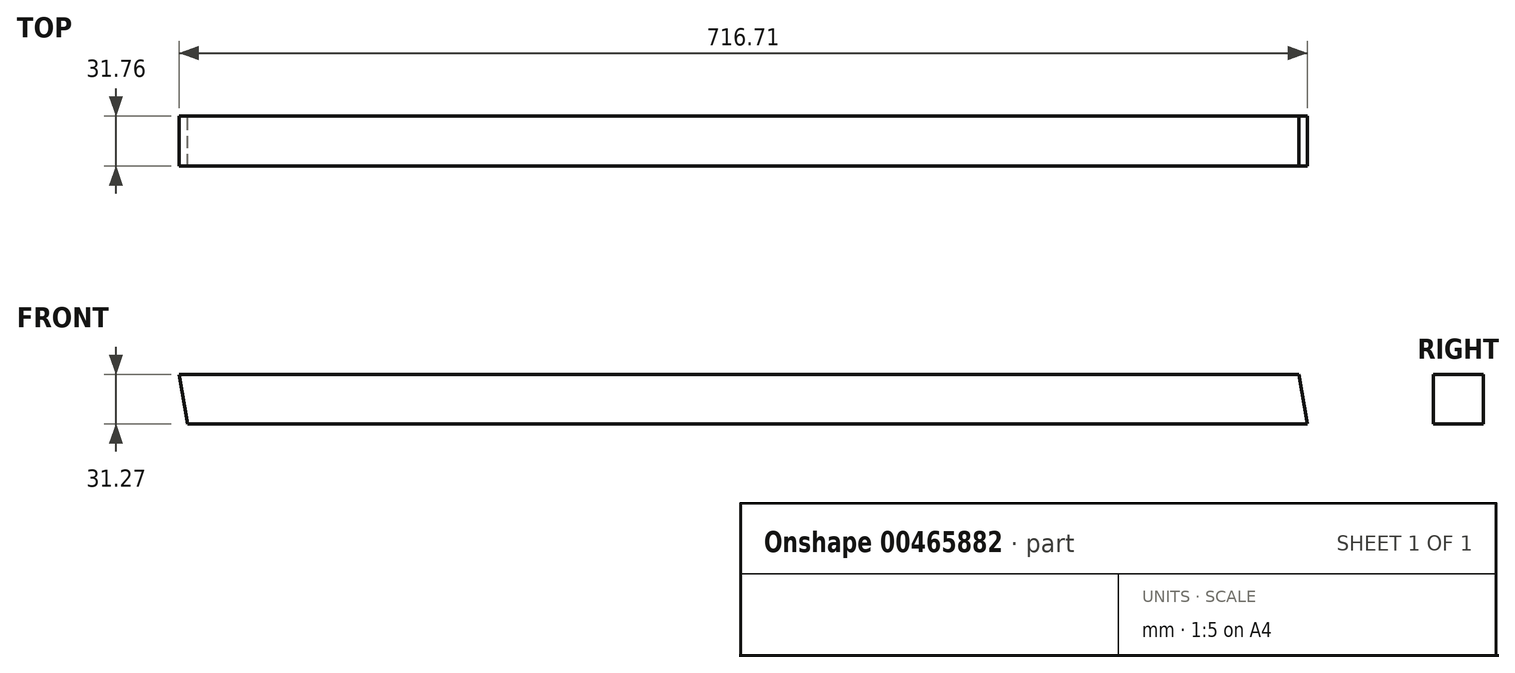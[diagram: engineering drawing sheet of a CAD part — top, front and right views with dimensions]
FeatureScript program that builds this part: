
annotation { "Feature Type Name" : "Feature", "Feature Type Description" : "" }
export const myFeature = defineFeature(function(context is Context, id is Id, definition is map)
    precondition{}
    {
        {
            var Q0;
            Q0=qCreatedBy(makeId("Front.planeOp"),FACE);
            var sketch = newSketch(context, id + "F0", { "sketchPlane" : qUnion([Q0])});
            skLineSegment(sketch, "E0", {"start": v(0, 0) * mm, "end": v(-711.2, 0) * mm});
            skLineSegment(sketch, "E1", {"start": v(-711.2, 0) * mm, "end": v(-705.69, -31.27) * mm});
            skLineSegment(sketch, "E2", {"start": v(0, 0) * mm, "end": v(5.51, -31.27) * mm});
            skLineSegment(sketch, "E3", {"start": v(-705.69, -31.27) * mm, "end": v(5.51, -31.27) * mm});
            skSolve(sketch);
        }
        {
            var Q0;
            Q0=makeQuery(id+"F0.imprint","IMPRINT",FACE,{"disambiguationData":[TD([[makeQuery(id+"F0.imprint","IMPRINT",EDGE,{"derivedFrom":sQuery(id+"F0.wireOp",EDGE,"E0")}),1.0]])]});
            extrude(context, id + "F1", {"entities" : qUnion([Q0]), "endBound" : BoundingType.SYMMETRIC, "depth" : 31.75 * mm});
        }
    });
